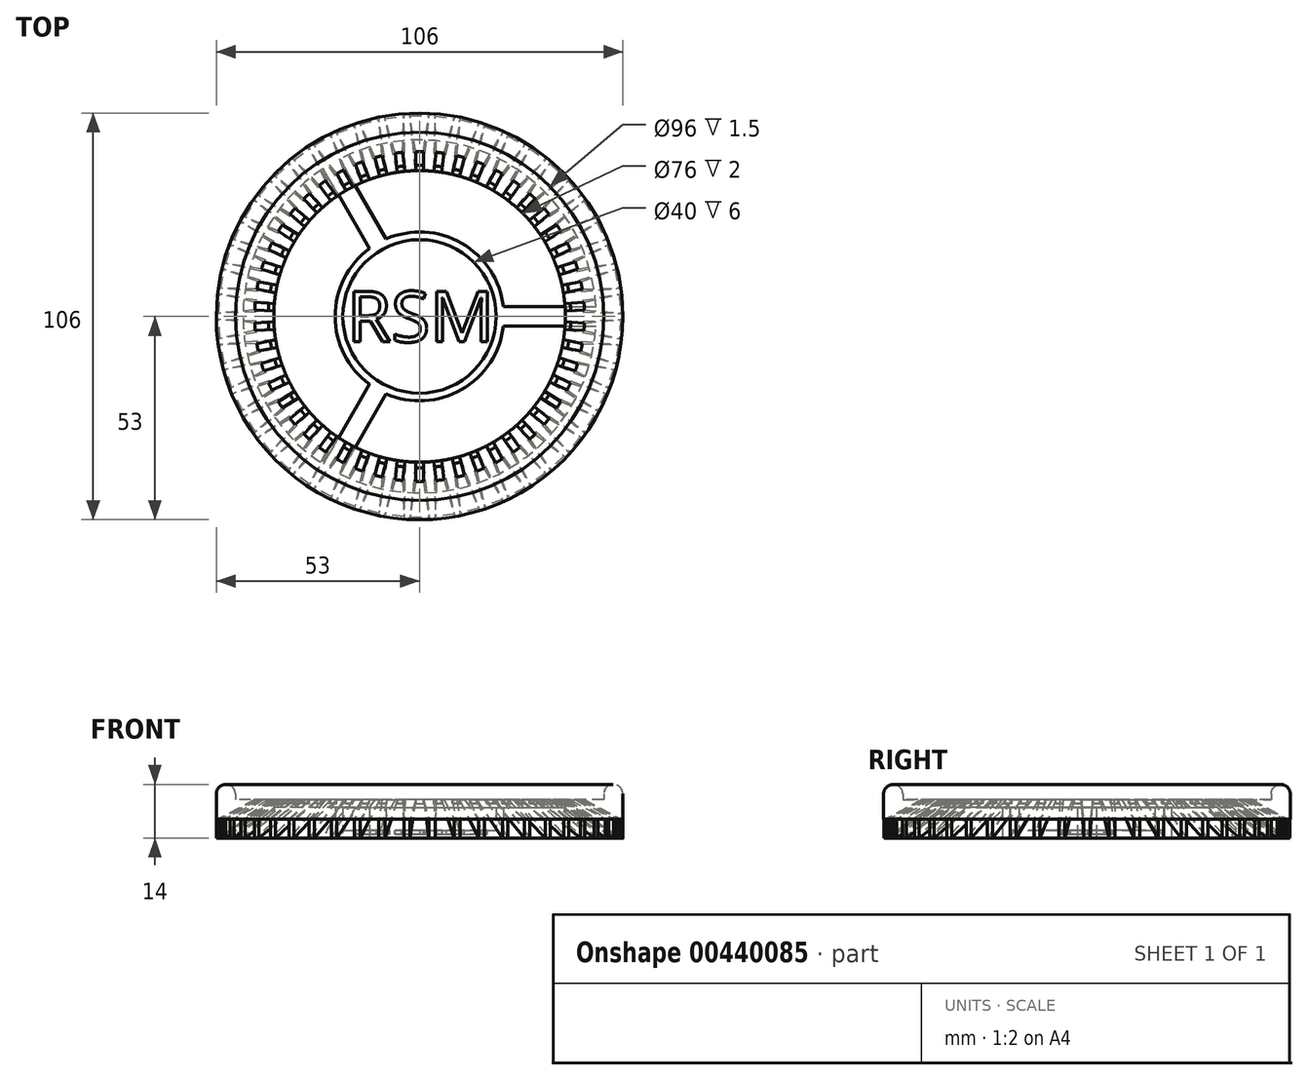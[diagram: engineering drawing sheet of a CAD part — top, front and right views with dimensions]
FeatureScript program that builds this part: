
annotation { "Feature Type Name" : "Feature", "Feature Type Description" : "" }
export const myFeature = defineFeature(function(context is Context, id is Id, definition is map)
    precondition{}
    {
        {
            var Q0;
            Q0=qCreatedBy(makeId("Top.planeOp"),FACE);
            var sketch = newSketch(context, id + "F0", { "sketchPlane" : qUnion([Q0])});
            skCircle(sketch, "E0", {"center": v(0, 0) * mm, "radius": 48 * mm});
            skCircle(sketch, "E1", {"center": v(0, 0) * mm, "radius": 53 * mm});
            skCircle(sketch, "E2", {"center": v(0, 0) * mm, "radius": 43 * mm});
            skCircle(sketch, "E3", {"center": v(0, 0) * mm, "radius": 38 * mm});
            skLineSegment(sketch, "E4", {"start": v(-1, -37.99) * mm, "end": v(-1, -42.99) * mm});
            skLineSegment(sketch, "E5", {"start": v(1, -37.99) * mm, "end": v(1, -42.99) * mm});
            skSolve(sketch);
        }
        {
            var Q0;
            Q0=makeQuery(id+"F0.imprint","IMPRINT",FACE,{"disambiguationData":[TD([[makeQuery(id+"F0.imprint","IMPRINT",EDGE,{"derivedFrom":sQuery(id+"F0.wireOp",EDGE,"E0")}),-1.0]])]});
            extrude(context, id + "F1", {"entities" : qUnion([Q0]), "depth" : 4 * mm});
        }
        {
            var Q0;
            Q0 = qSketchRegion(id + "F0", true);
            var Q1;
            Q1=makeQuery(id+"F0.imprint","IMPRINT",FACE,{"disambiguationData":[TD([[makeQuery(id+"F0.imprint","IMPRINT",EDGE,{"derivedFrom":sQuery(id+"F0.wireOp",EDGE,"E0")}),1.0]])]});
            var Q2;
            {var subQ0=sQuery(id+"F0.wireOp",EDGE,"E4");Q2=makeQuery(id+"F0.imprint","IMPRINT",FACE,{"disambiguationData":[TD([[makeQuery(id+"F0.imprint","IMPRINT",EDGE,{"derivedFrom":subQ0}),-1.0]])]});}
            var Q3;
            {var subQ0=sQuery(id+"F0.wireOp",EDGE,"E4");Q3=makeQuery(id+"F0.imprint","IMPRINT",FACE,{"disambiguationData":[TD([[makeQuery(id+"F0.imprint","IMPRINT",EDGE,{"derivedFrom":subQ0}),1.0]])]});}
            extrude(context, id + "F2", {"entities" : qUnion([Q0, Q1, Q2, Q3]), "operationType" : NewBodyOperationType.ADD, "oppositeDirection" : true, "depth" : 10 * mm});
        }
        {
            var Q0;
            Q0=qCreatedBy(makeId("Front.planeOp"),FACE);
            cPlane(context, id + "F3", {"entities" : qUnion([Q0]), "cplaneType" : CPlaneType.OFFSET, "offset" : 52.3 * mm, "width" : 150 * mm, "height" : 150 * mm});
        }
        {
            var Q0;
            Q0=qCreatedBy(id+"F3.planeOp",FACE);
            var sketch = newSketch(context, id + "F4", { "sketchPlane" : qUnion([Q0])});
            skLineSegment(sketch, "E6.0", {"start": v(-53, -10) * mm, "end": v(53, -10) * mm});
            skLineSegment(sketch, "E7.0", {"start": v(-53, 4) * mm, "end": v(53, 4) * mm});
            skLineSegment(sketch, "E8.bottom", {"start": v(2.5, -10) * mm, "end": v(-2.5, -10) * mm});
            skLineSegment(sketch, "E8.top", {"start": v(2.5, -5) * mm, "end": v(-2.5, -5) * mm});
            skLineSegment(sketch, "E8.left", {"start": v(2.5, -10) * mm, "end": v(2.5, -5) * mm});
            skLineSegment(sketch, "E8.right", {"start": v(-2.5, -10) * mm, "end": v(-2.5, -5) * mm});
            skPoint(sketch, "E8.middle", {"position": v(0, -7.5) * mm});
            skSolve(sketch);
        }
        {
            var Q0;
            Q0 = qSketchRegion(id + "F4", true);
            extrude(context, id + "F5", {"entities" : qUnion([Q0]), "operationType" : NewBodyOperationType.REMOVE, "depth" : 25 * mm});
        }
        {
            var Q0;
            {var subQ0=sQuery(id+"F0.wireOp",EDGE,"E4");Q0=makeQuery(id+"F0.imprint","IMPRINT",FACE,{"disambiguationData":[TD([[makeQuery(id+"F0.imprint","IMPRINT",EDGE,{"derivedFrom":subQ0}),1.0]])]});}
            extrude(context, id + "F6", {"entities" : qUnion([Q0]), "operationType" : NewBodyOperationType.REMOVE, "oppositeDirection" : true, "depth" : 1 * mm});
        }
        {
            var Q1;
            {var subQ0=sQuery(id+"F0.wireOp",EDGE,"E4");Q1=makeQuery(id+"F0.imprint","IMPRINT",FACE,{"disambiguationData":[TD([[makeQuery(id+"F0.imprint","IMPRINT",EDGE,{"derivedFrom":subQ0}),1.0]])]});}
            var Q2;
            Q2=makeQuery(id+"F5.boolean.opBoolean","COPY",FACE,{"derivedFrom":makeQuery(id+"F5.opExtrude","CAP_FACE",FACE,{"disambiguationData":[OSD([sQuery(id+"F4.wireOp",EDGE,"E8.bottom"),sQuery(id+"F4.wireOp",EDGE,"E8.top"),sQuery(id+"F4.wireOp",EDGE,"E8.left"),sQuery(id+"F4.wireOp",EDGE,"E8.right")])],"isStart":true})});
            loft(context, id + "F7", {"operationType" : NewBodyOperationType.REMOVE, "sheetProfilesArray" : [{ "sheetProfileEntities" : qUnion([Q1]) }, { "sheetProfileEntities" : qUnion([Q2]) }]});
        }
        {
            var Q0;
            {var subQ0=sQuery(id+"F0.wireOp",EDGE,"E1");Q0=makeQuery(id+"F5.boolean.opBoolean","INTERSECT",EDGE,{"derivedFrom":[makeQuery(id+"F2.boolean.opBoolean","MERGE",FACE,{"derivedFrom":[makeQuery(id+"F1.opExtrude","SWEPT_FACE",FACE,{"disambiguationData":[OSD([subQ0])]}),makeQuery(id+"F2.opExtrude","SWEPT_FACE",FACE,{"disambiguationData":[OSD([subQ0])]})]}),makeQuery(id+"F5.opExtrude","SWEPT_FACE",FACE,{"disambiguationData":[OSD([sQuery(id+"F4.wireOp",EDGE,"E8.right")])]})]});}
            var Q1;
            {var subQ0=sQuery(id+"F0.wireOp",EDGE,"E1");Q1=makeQuery(id+"F5.boolean.opBoolean","INTERSECT",EDGE,{"derivedFrom":[makeQuery(id+"F2.boolean.opBoolean","MERGE",FACE,{"derivedFrom":[makeQuery(id+"F1.opExtrude","SWEPT_FACE",FACE,{"disambiguationData":[OSD([subQ0])]}),makeQuery(id+"F2.opExtrude","SWEPT_FACE",FACE,{"disambiguationData":[OSD([subQ0])]})]}),makeQuery(id+"F5.opExtrude","SWEPT_FACE",FACE,{"disambiguationData":[OSD([sQuery(id+"F4.wireOp",EDGE,"E8.left")])]})]});}
            fillet(context, id + "F8", {"entities" : qUnion([Q0, Q1]), "radius" : .8 * mm, "tangentPropagation" : true, "allowEdgeOverflow" : false});
        }
        {
            var Q0;
            {var subQ0=sQuery(id+"F4.wireOp",EDGE,"E8.left");var subQ1=sQuery(id+"F0.wireOp",EDGE,"E5");Q0=makeQuery(id+"F7.boolean.opBoolean","MERGE",FACE,{"derivedFrom":[makeQuery(id+"F5.boolean.opBoolean","COPY",FACE,{"derivedFrom":makeQuery(id+"F5.opExtrude","SWEPT_FACE",FACE,{"disambiguationData":[OSD([subQ0])]})}),makeQuery(id+"F6.boolean.opBoolean","COPY",FACE,{"derivedFrom":makeQuery(id+"F6.opExtrude","SWEPT_FACE",FACE,{"disambiguationData":[OSD([subQ1])]})}),makeQuery(id+"F7.opLoft","SWEPT_FACE",FACE,{"disambiguationData":[OSD([sQuery(id+"F0.wireOp",EDGE,"E2"),sQuery(id+"F0.wireOp",EDGE,"E3"),subQ1,sQuery(id+"F4.wireOp",EDGE,"E8.bottom"),sQuery(id+"F4.wireOp",EDGE,"E8.top"),subQ0])]})]});}
            var Q1;
            Q1=makeQuery(id+"F7.boolean.opBoolean","COPY",FACE,{"derivedFrom":makeQuery(id+"F7.opLoft","SWEPT_FACE",FACE,{"disambiguationData":[OSD([sQuery(id+"F0.wireOp",EDGE,"E3"),sQuery(id+"F0.wireOp",EDGE,"E4"),sQuery(id+"F0.wireOp",EDGE,"E5"),sQuery(id+"F4.wireOp",EDGE,"E8.bottom"),sQuery(id+"F4.wireOp",EDGE,"E8.left"),sQuery(id+"F4.wireOp",EDGE,"E8.right")])]})});
            var Q2;
            {var subQ0=sQuery(id+"F4.wireOp",EDGE,"E8.right");var subQ1=sQuery(id+"F0.wireOp",EDGE,"E4");Q2=makeQuery(id+"F7.boolean.opBoolean","MERGE",FACE,{"derivedFrom":[makeQuery(id+"F5.boolean.opBoolean","COPY",FACE,{"derivedFrom":makeQuery(id+"F5.opExtrude","SWEPT_FACE",FACE,{"disambiguationData":[OSD([subQ0])]})}),makeQuery(id+"F6.boolean.opBoolean","COPY",FACE,{"derivedFrom":makeQuery(id+"F6.opExtrude","SWEPT_FACE",FACE,{"disambiguationData":[OSD([subQ1])]})}),makeQuery(id+"F7.opLoft","SWEPT_FACE",FACE,{"disambiguationData":[OSD([sQuery(id+"F0.wireOp",EDGE,"E2"),sQuery(id+"F0.wireOp",EDGE,"E3"),subQ1,sQuery(id+"F4.wireOp",EDGE,"E8.bottom"),sQuery(id+"F4.wireOp",EDGE,"E8.top"),subQ0])]})]});}
            var Q3;
            Q3=makeQuery(id+"F7.boolean.opBoolean","COPY",FACE,{"derivedFrom":makeQuery(id+"F7.opLoft","SWEPT_FACE",FACE,{"disambiguationData":[OSD([sQuery(id+"F0.wireOp",EDGE,"E2"),sQuery(id+"F0.wireOp",EDGE,"E4"),sQuery(id+"F0.wireOp",EDGE,"E5"),sQuery(id+"F4.wireOp",EDGE,"E8.top"),sQuery(id+"F4.wireOp",EDGE,"E8.left"),sQuery(id+"F4.wireOp",EDGE,"E8.right")])]})});
            var Q4;
            Q4=makeQuery(id+"F5.boolean.opBoolean","COPY",FACE,{"derivedFrom":makeQuery(id+"F5.opExtrude","SWEPT_FACE",FACE,{"disambiguationData":[OSD([sQuery(id+"F4.wireOp",EDGE,"E8.top")])]})});
            var Q5;
            Q5=makeQuery(id+"F6.boolean.opBoolean","COPY",FACE,{"derivedFrom":makeQuery(id+"F6.opExtrude","CAP_FACE",FACE,{"disambiguationData":[OSD([sQuery(id+"F0.wireOp",EDGE,"E2"),sQuery(id+"F0.wireOp",EDGE,"E3"),sQuery(id+"F0.wireOp",EDGE,"E4"),sQuery(id+"F0.wireOp",EDGE,"E5")])],"isStart":false})});
            var Q6;
            Q6=makeQuery(id+"F7.boolean.opBoolean","COPY",FACE,{"derivedFrom":makeQuery(id+"F7.opLoft","SWEPT_FACE",FACE,{"disambiguationData":[OSD([sQuery(id+"F0.wireOp",EDGE,"E2"),sQuery(id+"F0.wireOp",EDGE,"E3"),sQuery(id+"F0.wireOp",EDGE,"E4"),sQuery(id+"F4.wireOp",EDGE,"E8.bottom"),sQuery(id+"F4.wireOp",EDGE,"E8.top"),sQuery(id+"F4.wireOp",EDGE,"E8.right")])]})});
            var Q7;
            Q7=makeQuery(id+"F7.boolean.opBoolean","COPY",FACE,{"derivedFrom":makeQuery(id+"F7.opLoft","SWEPT_FACE",FACE,{"disambiguationData":[OSD([sQuery(id+"F0.wireOp",EDGE,"E2"),sQuery(id+"F0.wireOp",EDGE,"E3"),sQuery(id+"F0.wireOp",EDGE,"E5"),sQuery(id+"F4.wireOp",EDGE,"E8.bottom"),sQuery(id+"F4.wireOp",EDGE,"E8.top"),sQuery(id+"F4.wireOp",EDGE,"E8.left")])]})});
            var Q8;
            Q8=makeQuery(id+"F8.opFillet","BLEND_FACE",FACE,{"disambiguationData":[OSD([sQuery(id+"F0.wireOp",EDGE,"E1"),sQuery(id+"F4.wireOp",EDGE,"E8.right")])]});
            var Q9;
            Q9=makeQuery(id+"F8.opFillet","BLEND_FACE",FACE,{"disambiguationData":[OSD([sQuery(id+"F0.wireOp",EDGE,"E1"),sQuery(id+"F4.wireOp",EDGE,"E8.left")])]});
            var Q10;
            Q10=makeQuery(id+"F1.opExtrude","CAP_EDGE",EDGE,{"disambiguationData":[OSD([sQuery(id+"F0.wireOp",EDGE,"E1")])],"isStart":false});
            circularPattern(context, id + "F9", {"patternType" : PatternType.FACE, "faces" : qUnion([Q0, Q1, Q2, Q3, Q4, Q5, Q6, Q7, Q8, Q9]), "axis" : qUnion([Q10]), "angle" : 360 * degree, "instanceCount" : 50, "equalSpace" : true});
        }
        {
            var Q0;
            Q0=makeQuery(id+"F1.opExtrude","CAP_EDGE",EDGE,{"disambiguationData":[OSD([sQuery(id+"F0.wireOp",EDGE,"E0")])],"isStart":false});
            var Q1;
            Q1=makeQuery(id+"F1.opExtrude","CAP_EDGE",EDGE,{"disambiguationData":[OSD([sQuery(id+"F0.wireOp",EDGE,"E1")])],"isStart":false});
            fillet(context, id + "F10", {"entities" : qUnion([Q0, Q1]), "radius" : 2.5 * mm, "tangentPropagation" : true, "allowEdgeOverflow" : false});
        }
        {
            var Q0;
            Q0=makeQuery(id+"F2.opExtrude","CAP_EDGE",EDGE,{"disambiguationData":[OSD([sQuery(id+"F0.wireOp",EDGE,"E3")])],"isStart":false});
            chamfer(context, id + "F11", {"entities" : qUnion([Q0]), "width" : 8 * mm, "tangentPropagation" : true});
        }
        {
            var Q0;
            Q0=makeQuery(id+"F2.opExtrude","CAP_FACE",FACE,{"disambiguationData":[OSD([sQuery(id+"F0.wireOp",EDGE,"E1"),sQuery(id+"F0.wireOp",EDGE,"E3")])],"isStart":false});
            var sketch = newSketch(context, id + "F12", { "sketchPlane" : qUnion([Q0])});
            skCircle(sketch, "E9", {"center": v(0, 0) * mm, "radius": 20 * mm});
            skCircle(sketch, "E10", {"center": v(0, 0) * mm, "radius": 22 * mm});
            skSolve(sketch);
        }
        {
            var Q0;
            Q0=makeQuery(id+"F12.imprint","IMPRINT",FACE,{"disambiguationData":[TD([[makeQuery(id+"F12.imprint","IMPRINT",EDGE,{"derivedFrom":sQuery(id+"F12.wireOp",EDGE,"E9")}),-1.0]])]});
            extrude(context, id + "F13", {"entities" : qUnion([Q0]), "oppositeDirection" : true, "depth" : 8 * mm});
        }
        {
            var Q0;
            Q0=makeQuery(id+"F12.imprint","IMPRINT",FACE,{"disambiguationData":[TD([[makeQuery(id+"F12.imprint","IMPRINT",EDGE,{"derivedFrom":sQuery(id+"F12.wireOp",EDGE,"E9")}),1.0]])]});
            extrude(context, id + "F14", {"entities" : qUnion([Q0]), "operationType" : NewBodyOperationType.ADD, "oppositeDirection" : true, "depth" : 2 * mm});
        }
        {
            var Q0;
            Q0=qCreatedBy(makeId("Right.planeOp"),FACE);
            cPlane(context, id + "F15", {"entities" : qUnion([Q0]), "cplaneType" : CPlaneType.OFFSET, "offset" : 25 * mm, "width" : 150 * mm, "height" : 150 * mm});
        }
        {
            var Q0;
            Q0=qCreatedBy(id+"F15.planeOp",FACE);
            var sketch = newSketch(context, id + "F16", { "sketchPlane" : qUnion([Q0])});
            skLineSegment(sketch, "E11.0", {"start": v(22, -2) * mm, "end": v(-22, -2) * mm});
            skLineSegment(sketch, "E12.0", {"start": v(22, -10) * mm, "end": v(-22, -10) * mm});
            skLineSegment(sketch, "E13.bottom", {"start": v(-2.5, -2) * mm, "end": v(2.5, -2) * mm});
            skLineSegment(sketch, "E13.top", {"start": v(-2.5, -10) * mm, "end": v(2.5, -10) * mm});
            skLineSegment(sketch, "E13.left", {"start": v(-2.5, -2) * mm, "end": v(-2.5, -10) * mm});
            skLineSegment(sketch, "E13.right", {"start": v(2.5, -2) * mm, "end": v(2.5, -10) * mm});
            skSolve(sketch);
        }
        {
            var Q0;
            Q0 = qSketchRegion(id + "F16", true);
            var Q1;
            Q1=makeQuery(id+"F13.opExtrude","SWEPT_BODY",BODY,{"disambiguationData":[OSD([sQuery(id+"F12.wireOp",EDGE,"E9"),sQuery(id+"F12.wireOp",EDGE,"E10")])]});
            var Q2;
            Q2=makeQuery(id+"F1.opExtrude","SWEPT_BODY",BODY,{"disambiguationData":[OSD([sQuery(id+"F0.wireOp",EDGE,"E0"),sQuery(id+"F0.wireOp",EDGE,"E1")])]});
            extrude(context, id + "F17", {"entities" : qUnion([Q0]), "endBound" : BoundingType.UP_TO_BODY, "oppositeDirection" : true, "endBoundEntityBody" : qUnion([Q1]), "depth" : 25 * mm, "hasSecondDirection" : true, "secondDirectionBound" : SecondDirectionBoundingType.UP_TO_BODY, "secondDirectionOppositeDirection" : false, "secondDirectionBoundEntityBody" : qUnion([Q2]), "secondDirectionDepth" : 25 * mm});
        }
        {
            var Q0;
            Q0=makeQuery(id+"F17.opExtrude","SWEPT_BODY",BODY,{"disambiguationData":[OSD([sQuery(id+"F16.wireOp",EDGE,"E13.bottom"),sQuery(id+"F16.wireOp",EDGE,"E13.top"),sQuery(id+"F16.wireOp",EDGE,"E13.left"),sQuery(id+"F16.wireOp",EDGE,"E13.right")])]});
            var Q1;
            Q1=makeQuery(id+"F13.opExtrude","CAP_EDGE",EDGE,{"disambiguationData":[OSD([sQuery(id+"F12.wireOp",EDGE,"E9")])],"isStart":false});
            circularPattern(context, id + "F18", {"operationType" : NewBodyOperationType.ADD, "entities" : qUnion([Q0]), "axis" : qUnion([Q1]), "angle" : 360 * degree, "instanceCount" : 3, "equalSpace" : true});
        }
        {
            var Q0;
            Q0=qCreatedBy(makeId("Top.planeOp"),FACE);
            cPlane(context, id + "F19", {"entities" : qUnion([Q0]), "cplaneType" : CPlaneType.OFFSET, "offset" : 8 * mm, "oppositeDirection" : true, "width" : 150 * mm, "height" : 150 * mm});
        }
        {
            var Q0;
            Q0=qCreatedBy(id+"F19.planeOp",FACE);
            var sketch = newSketch(context, id + "F20", { "sketchPlane" : qUnion([Q0])});
            skCircle(sketch, "E14.0", {"center": v(0, 0) * mm, "radius": 20 * mm, "construction": true});
            skText(sketch, "E15", { "text": "RSM", "fontName": "NotoSans-Regular.ttf"});
            const initialGuessF20  = {"E15": [-0.01887, -0.00664, 1, 0, 0.01328]};
            skSetInitialGuess(sketch, initialGuessF20);
            skSolve(sketch);
        }
        {
            var Q0;
            Q0 = qSketchRegion(id + "F20", true);
            extrude(context, id + "F21", {"entities" : qUnion([Q0]), "operationType" : NewBodyOperationType.REMOVE, "oppositeDirection" : true, "depth" : 1 * mm});
        }
    });
